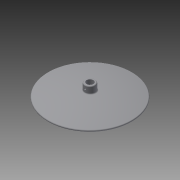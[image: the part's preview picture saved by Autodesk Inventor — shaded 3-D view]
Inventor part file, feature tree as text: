
AUTODESK INVENTOR PART (.ipt)
format: ipt  version: 2014 (Build 180170000, 170)  size: 141,312 bytes
history: native  units: in
note: dims shown in document units (in); Inventor stores cm internally (conversion verified against a paired STEP export)
features: fillet x3, sketch x3, plane x2, extrude x2, revolve x1
ambient origin geometry x8: Origin, YZ Plane, XZ Plane, XY Plane, X Axis, Y Axis, Z Axis, Center Point
bodies: Solid1 (feature_tree)
feature tree (11):
  revolve  "Revolution1"  [1 undecoded]
  fillet  "Fillet1"  Radius=0.25in
  fillet  "Fillet2"  [1 undecoded]
  plane  "Work Plane1"
  extrude  "Extrusion1"  Depth=0.0625in
  plane  "Work Plane2"
  extrude  "Extrusion2"  Depth=0.0625in
  fillet  "Fillet3"  Radius=0.5in
  sketch  "Sketch1"  dims[d0=24.0in d1=11.75in d2=0.25in d3=90.0deg]
  sketch  "Sketch2"  dims[d4=5.0in d5=0.0625in]
  sketch  "Sketch3"  dims[d6=0.5in d7=0.75in d8=0.5in d9=0.1in d10=0.0in d11=0.0in d12=0.125in d13=12.5in d14=1.0in d15=0.0in d16=0.0625in]
note: 2 required parameter values undecoded (feature->parameter linkage not recoverable at this tier; creation-order binding heuristic only, values carry confidence <= 0.55)